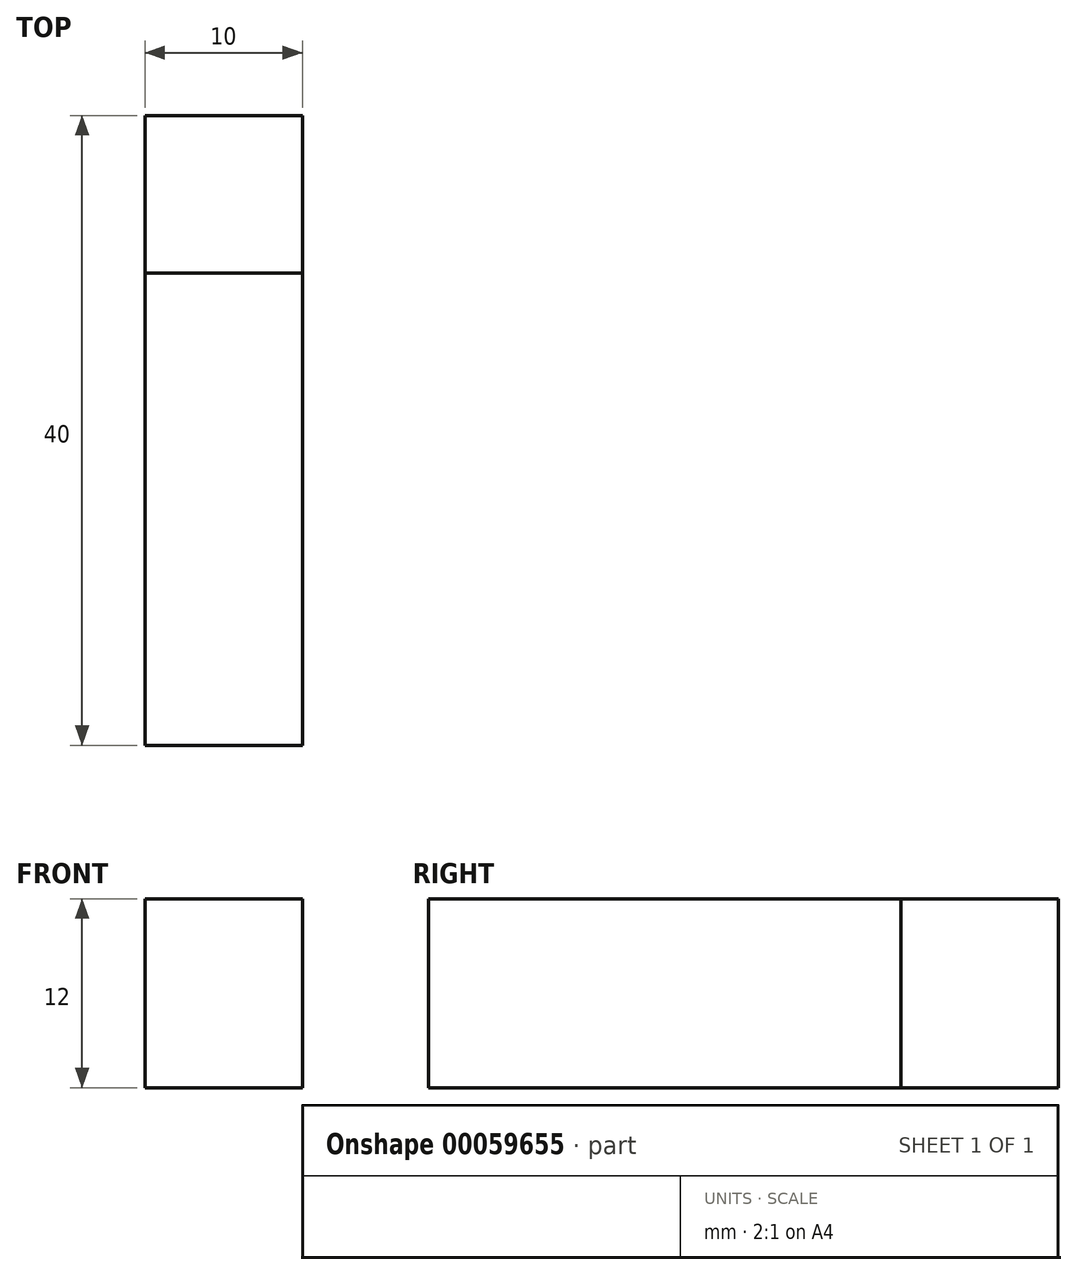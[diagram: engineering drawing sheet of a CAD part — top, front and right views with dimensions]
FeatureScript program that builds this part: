
annotation { "Feature Type Name" : "Feature", "Feature Type Description" : "" }
export const myFeature = defineFeature(function(context is Context, id is Id, definition is map)
    precondition{}
    {
        {
            var Q0;
            Q0=qCreatedBy(makeId("Front.planeOp"),FACE);
            var sketch = newSketch(context, id + "F0", { "sketchPlane" : qUnion([Q0])});
            skLineSegment(sketch, "E0.bottom", {"start": v(0, 0) * mm, "end": v(10, 0) * mm});
            skLineSegment(sketch, "E0.top", {"start": v(0, 12) * mm, "end": v(10, 12) * mm});
            skLineSegment(sketch, "E0.left", {"start": v(0, 0) * mm, "end": v(0, 12) * mm});
            skLineSegment(sketch, "E0.right", {"start": v(10, 0) * mm, "end": v(10, 12) * mm});
            skSolve(sketch);
        }
        {
            var Q0;
            Q0 = qSketchRegion(id + "F0", true);
            extrude(context, id + "F1", {"entities" : qUnion([Q0]), "depth" : 30 * mm});
        }
        {
            var Q0;
            Q0=makeQuery(id+"F1.opExtrude","CAP_FACE",FACE,{"disambiguationData":[OSD([sQuery(id+"F0.wireOp",EDGE,"E0.bottom"),sQuery(id+"F0.wireOp",EDGE,"E0.top"),sQuery(id+"F0.wireOp",EDGE,"E0.left"),sQuery(id+"F0.wireOp",EDGE,"E0.right")])],"isStart":true});
            extrude(context, id + "F2", {"entities" : qUnion([Q0]), "depth" : 10 * mm});
        }
    });
